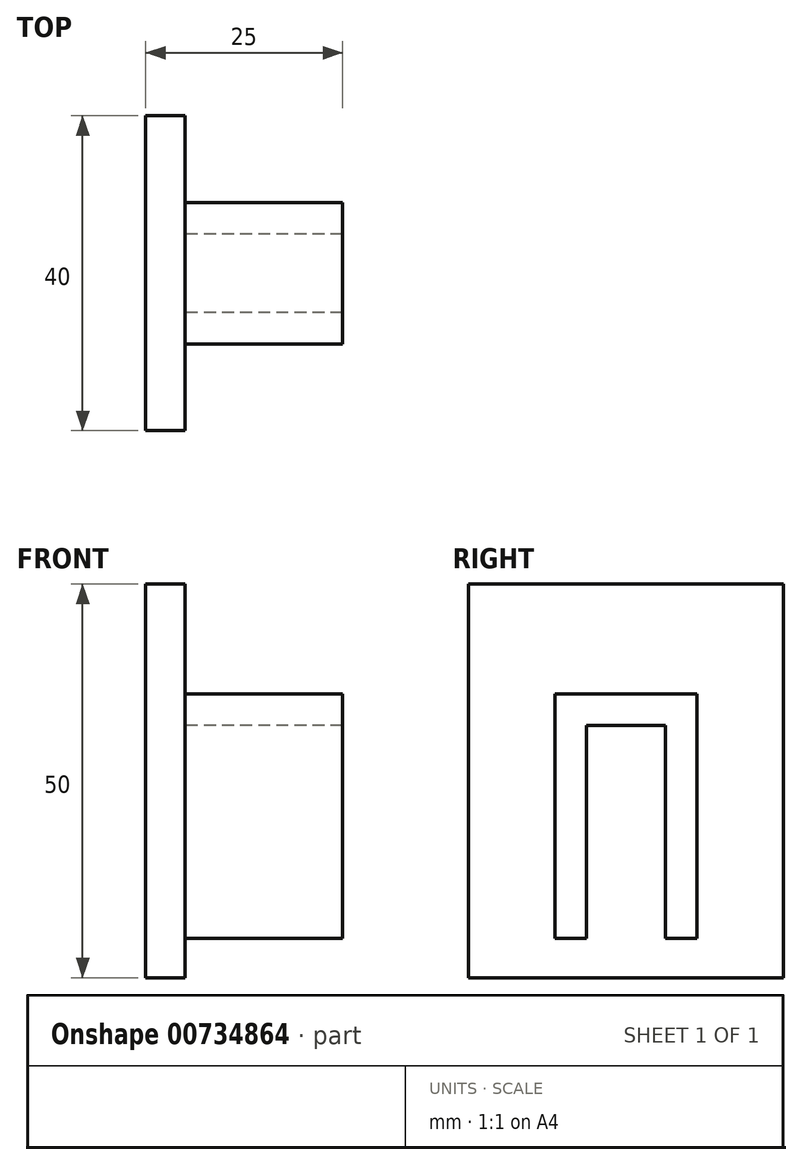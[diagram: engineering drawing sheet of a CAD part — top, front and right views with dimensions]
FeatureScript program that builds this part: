
annotation { "Feature Type Name" : "Feature", "Feature Type Description" : "" }
export const myFeature = defineFeature(function(context is Context, id is Id, definition is map)
    precondition{}
    {
        {
            var Q0;
            Q0=qCreatedBy(makeId("Right.planeOp"),FACE);
            var sketch = newSketch(context, id + "F0", { "sketchPlane" : qUnion([Q0])});
            skLineSegment(sketch, "E0.bottom", {"start": v(0, 0) * mm, "end": v(40, 0) * mm});
            skLineSegment(sketch, "E0.top", {"start": v(0, 50) * mm, "end": v(40, 50) * mm});
            skLineSegment(sketch, "E0.left", {"start": v(0, 0) * mm, "end": v(0, 50) * mm});
            skLineSegment(sketch, "E0.right", {"start": v(40, 0) * mm, "end": v(40, 50) * mm});
            skSolve(sketch);
        }
        {
            var Q0;
            Q0=makeQuery(id+"F0.imprint","IMPRINT",FACE,{"disambiguationData":[TD([[makeQuery(id+"F0.imprint","IMPRINT",EDGE,{"derivedFrom":sQuery(id+"F0.wireOp",EDGE,"E0.bottom")}),1.0]])]});
            extrude(context, id + "F1", {"entities" : qUnion([Q0]), "depth" : 5 * mm, "offsetDistance" : 25 * mm});
        }
        {
            var Q0;
            Q0=makeQuery(id+"F1.opExtrude","CAP_FACE",FACE,{"disambiguationData":[OSD([sQuery(id+"F0.wireOp",EDGE,"E0.bottom"),sQuery(id+"F0.wireOp",EDGE,"E0.top"),sQuery(id+"F0.wireOp",EDGE,"E0.left"),sQuery(id+"F0.wireOp",EDGE,"E0.right")])],"isStart":false});
            var sketch = newSketch(context, id + "F2", { "sketchPlane" : qUnion([Q0])});
            skPoint(sketch, "E1.0", {"position": v(20, 50) * mm});
            skLineSegment(sketch, "E2.0", {"start": v(11, 5) * mm, "end": v(11, 36.08) * mm});
            skLineSegment(sketch, "E3.0", {"start": v(29, 5) * mm, "end": v(29, 36.08) * mm});
            skLineSegment(sketch, "E4.0", {"start": v(15, 32.08) * mm, "end": v(25, 32.08) * mm});
            skLineSegment(sketch, "E5.0", {"start": v(11, 36.08) * mm, "end": v(29, 36.08) * mm});
            skLineSegment(sketch, "E6.0", {"start": v(15, 5) * mm, "end": v(15, 32.08) * mm});
            skLineSegment(sketch, "E7.0", {"start": v(25, 5) * mm, "end": v(25, 32.08) * mm});
            skPoint(sketch, "E8.0.start.orphan", {"position": v(0, 0) * mm});
            skPoint(sketch, "E9.0.start.orphan", {"position": v(40, 0) * mm});
            skPoint(sketch, "E10.orphan", {"position": v(0, 50) * mm});
            skPoint(sketch, "E11.0.end.orphan", {"position": v(40, 50) * mm});
            skLineSegment(sketch, "E12.0", {"start": v(11, 5) * mm, "end": v(15, 5) * mm});
            skLineSegment(sketch, "E13.trimOffspring", {"start": v(25, 5) * mm, "end": v(29, 5) * mm});
            skSolve(sketch);
        }
        {
            var Q0;
            Q0=makeQuery(id+"F2.imprint","IMPRINT",FACE,{"disambiguationData":[TD([[makeQuery(id+"F2.imprint","IMPRINT",EDGE,{"derivedFrom":sQuery(id+"F2.wireOp",EDGE,"E2.0")}),-1.0]])]});
            extrude(context, id + "F3", {"entities" : qUnion([Q0]), "operationType" : NewBodyOperationType.ADD, "depth" : 20 * mm, "offsetDistance" : 25 * mm});
        }
    });
